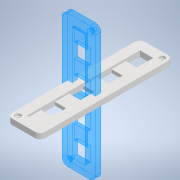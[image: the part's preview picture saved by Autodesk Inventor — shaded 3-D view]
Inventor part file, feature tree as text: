
AUTODESK INVENTOR PART (.ipt)
format: ipt  version: 2020 (Build 240168000, 168)  size: 224,256 bytes
history: native  units: mm
features: chamfer x16, other x3, direct_edit x1, draft x1, move_body x1
ambient origin geometry x8: Origin, YZ Plane, XZ Plane, XY Plane, X Axis, Y Axis, Z Axis, Center Point
bodies: Solid1 (feature_tree)
feature tree (22):
  other  "open_side.ipt"
  direct_edit  "Direct Edit1"
  chamfer  "Chamfer1"  Distance=10.0mm
  chamfer  "Chamfer2"  Distance=6.0mm
  chamfer  "Chamfer3"  Distance=2.0mm
  chamfer  "Chamfer4"  Distance=4.0mm
  chamfer  "Chamfer5"  Distance=2.0mm
  chamfer  "Chamfer6"  Distance=4.0mm
  chamfer  "Chamfer7"  Distance=2.0mm
  chamfer  "Chamfer8"  Distance=4.0mm
  chamfer  "Chamfer9"  Distance=2.0mm
  chamfer  "Chamfer10"  Distance=4.0mm
  chamfer  "Chamfer11"  Distance=2.0mm
  chamfer  "Chamfer12"  Distance=4.0mm
  chamfer  "Chamfer13"  Distance=2.0mm
  chamfer  "Chamfer14"  Distance=4.0mm
  chamfer  "Chamfer15"  Distance=2.0mm
  chamfer  "Chamfer16"  Distance=4.0mm
  draft  "FaceDraft2"
  other  "Solid1::open_side.ipt"
  other  "TaggingFeature1"
  move_body  "Move1"
